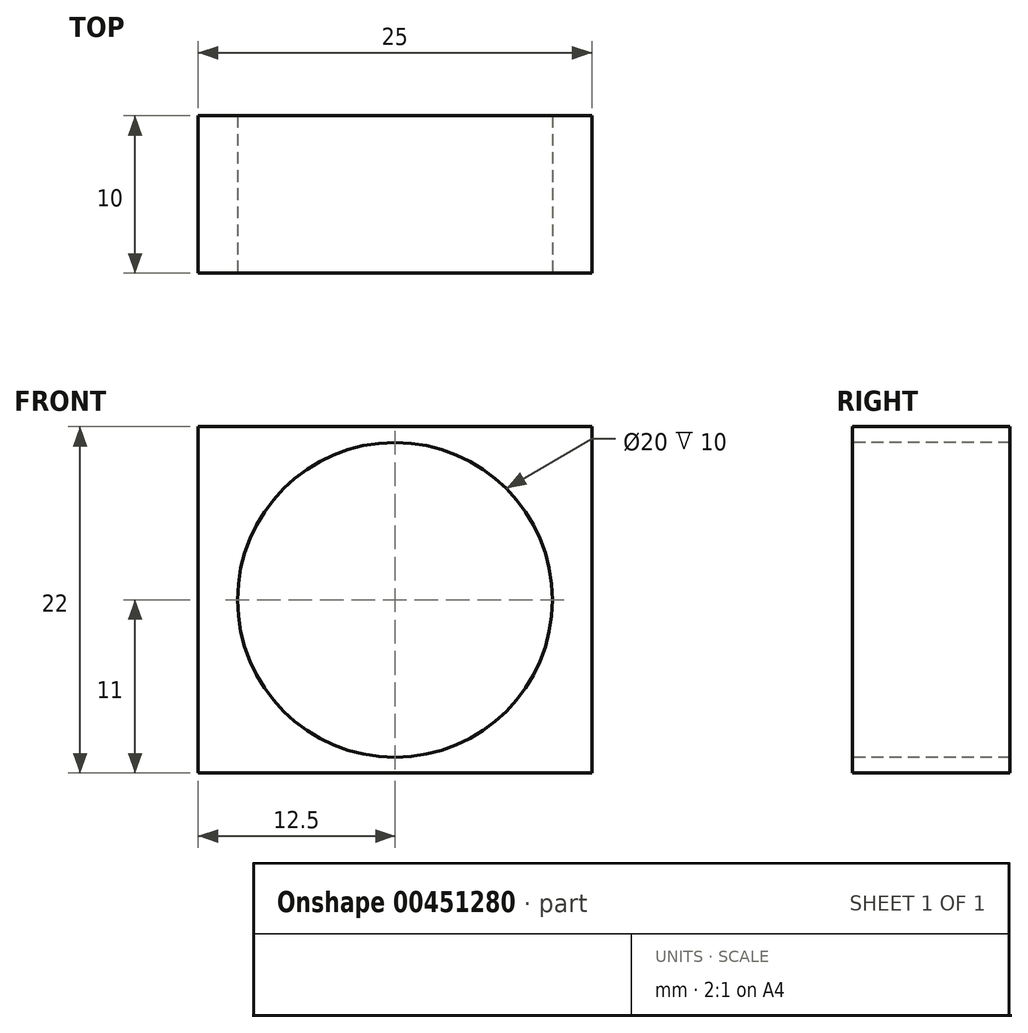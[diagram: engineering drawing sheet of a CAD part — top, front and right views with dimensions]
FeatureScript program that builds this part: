
annotation { "Feature Type Name" : "Feature", "Feature Type Description" : "" }
export const myFeature = defineFeature(function(context is Context, id is Id, definition is map)
    precondition{}
    {
        {
            var Q0;
            Q0=qCreatedBy(makeId("Front.planeOp"),FACE);
            var sketch = newSketch(context, id + "F0", { "sketchPlane" : qUnion([Q0])});
            skLineSegment(sketch, "E0.bottom", {"start": v(12.5, -11) * mm, "end": v(-12.5, -11) * mm});
            skLineSegment(sketch, "E0.top", {"start": v(12.5, 11) * mm, "end": v(-12.5, 11) * mm});
            skLineSegment(sketch, "E0.left", {"start": v(12.5, -11) * mm, "end": v(12.5, 11) * mm});
            skLineSegment(sketch, "E0.right", {"start": v(-12.5, -11) * mm, "end": v(-12.5, 11) * mm});
            skPoint(sketch, "E0.middle", {"position": v(0, 0) * mm});
            skCircle(sketch, "E1", {"center": v(0, 0) * mm, "radius": 10 * mm});
            skSolve(sketch);
        }
        {
            var Q0;
            Q0=makeQuery(id+"F0.imprint","IMPRINT",FACE,{"disambiguationData":[TD([[makeQuery(id+"F0.imprint","IMPRINT",EDGE,{"derivedFrom":sQuery(id+"F0.wireOp",EDGE,"E0.bottom")}),-1.0]])]});
            extrude(context, id + "F1", {"entities" : qUnion([Q0]), "oppositeDirection" : true, "depth" : 10 * mm});
        }
    });
